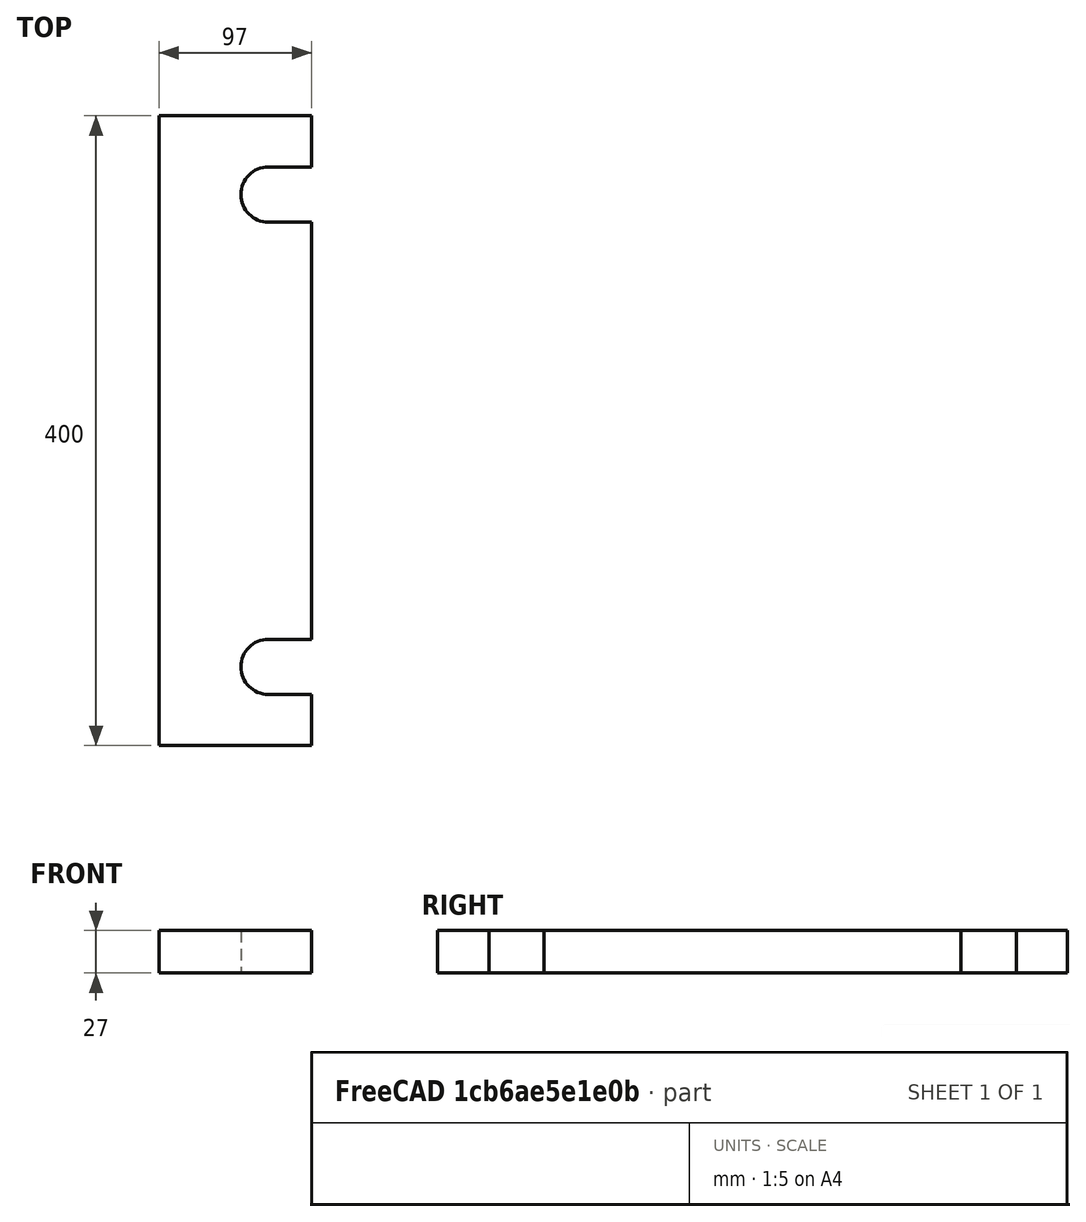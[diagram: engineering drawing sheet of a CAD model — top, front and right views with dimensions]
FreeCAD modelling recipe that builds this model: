
FCSTD DOCUMENT  (FreeCAD 0.20R25131 (Git))
Label: Seitenteil
License: All rights reserved
LicenseURL: http://en.wikipedia.org/wiki/All_rights_reserved
objects: Part::FeaturePython×8, Part::Box×2, App::FeaturePython×2, Part::MultiFuse×2, Part::Cylinder×1, Part::Mirroring×1, Part::Cut×1
note: 14 computed .brp shape members not serialized (recipe doc carries the construction recipe); baked Part::Feature solids carry a one-line shape summary decoded from their .brp
EXTERNAL_REF file=Grunddaten.FCStd obj=Spreadsheet

FEATURE [Part::Box] Box  label="Cube"
  AttacherType = Attacher::AttachEngine3D
  Height = 27
  Length = 97
  Width = 400
  expr: Length = <<Grunddaten>>#Spreadsheet.Hoehe
  expr: Width = <<Grunddaten>>#Spreadsheet.Plattenbreite
  expr: Height = <<Grunddaten>>#Spreadsheet.Plattendicke
FEATURE [App::FeaturePython] Constraints  # WARN: FeaturePython — macro-defined, semantics opaque (R4)
  _Version = 1
FEATURE [Part::Cylinder] Cylinder
  Angle = 360
  AttacherType = Attacher::AttachEngine3D
  FirstAngle = 0
  Height = 30
  Placement = pos=(69.5,50,0) rot=(0,0,1;0rad)
  Radius = 17.5
  SecondAngle = 0
  expr: .Placement.Base.x = <<Grunddaten>>#Spreadsheet.Hoehe - Radius - 10mm
FEATURE [Part::Box] Box001  label="Cube001"
  AttacherType = Attacher::AttachEngine3D
  Height = 30
  Length = 35
  Placement = pos=(69.5,32.5,0) rot=(0,0,1;0rad)
  Width = 35
  expr: Length = 2 * Cylinder.Radius
  expr: Width = 2 * Cylinder.Radius
  expr: .Placement.Base.x = <<Grunddaten>>#Spreadsheet.Hoehe - Length / 2 - 10mm
  expr: .Placement.Base.y = 50mm - Width / 2
FEATURE [Part::MultiFuse] Fusion
  Shapes = -> [Cylinder,Box001]
FEATURE [Part::Mirroring] Part__Mirroring  label="Fusion (Mirror #1)"
  Base = (0,200,0)
  Normal = (0,1,0)
  Source = -> Fusion
FEATURE [Part::MultiFuse] Fusion001
  Shapes = -> [Fusion,Part__Mirroring]
FEATURE [Part::Cut] Cut
  Base = -> Box
  Tool = -> Fusion001
FEATURE [Part::FeaturePython] Parts  # WARN: FeaturePython — macro-defined, semantics opaque (R4)
  Group = -> [Box,Cylinder,Box001,Fusion,Part__Mirroring,Fusion001,Cut]
  GroupMode = 0
FEATURE [Part::FeaturePython] Assembly  label="Seitenteil"  # WARN: FeaturePython — macro-defined, semantics opaque (R4)
  AutoRelax = true
  BuildShape = 0
  Freeze = false
  Group = -> [Constraints,Elements,Parts]
  Verbose = false
  _SolverType = 1
  _Version = 1
FEATURE [App::FeaturePython] Elements  # WARN: FeaturePython — macro-defined, semantics opaque (R4)
  Group = -> [Element,Element001,Element002,Element003,Element004,Element005]
FEATURE [Part::FeaturePython] Element  label="Oben"  # link proxy (typed FeaturePython)
  Detach = false
  LinkTransform = true
  LinkedObject = -> Box [Face2]
  _Parent = -> Elements
FEATURE [Part::FeaturePython] Element001  label="Seite"  # link proxy (typed FeaturePython)
  Detach = false
  LinkTransform = true
  LinkedObject = -> Box [Face6]
  _Parent = -> Elements
FEATURE [Part::FeaturePython] Element002  label="Vorne"  # link proxy (typed FeaturePython)
  Detach = false
  LinkTransform = true
  LinkedObject = -> Box [Face3]
  _Parent = -> Elements
FEATURE [Part::FeaturePython] Element003  # link proxy (typed FeaturePython)
  Detach = false
  LinkTransform = true
  LinkedObject = -> Box [Face5]
  _Parent = -> Elements
FEATURE [Part::FeaturePython] Element004  # link proxy (typed FeaturePython)
  Detach = false
  LinkTransform = true
  LinkedObject = -> Box [Face1]
  _Parent = -> Elements
FEATURE [Part::FeaturePython] Element005  # link proxy (typed FeaturePython)
  Detach = false
  LinkTransform = true
  LinkedObject = -> Box [Face4]
  _Parent = -> Elements
